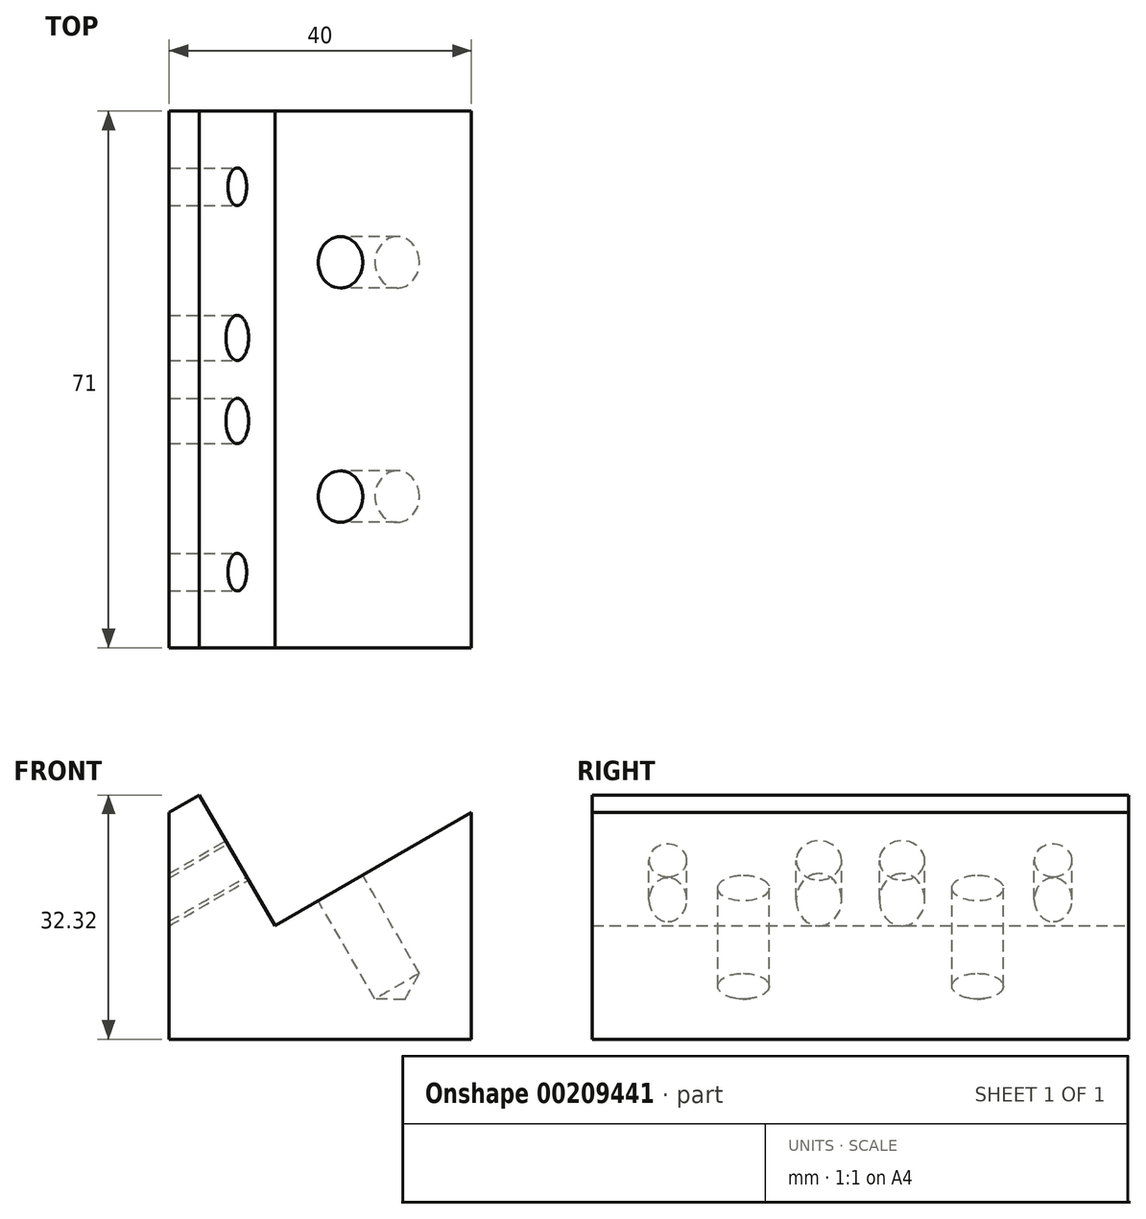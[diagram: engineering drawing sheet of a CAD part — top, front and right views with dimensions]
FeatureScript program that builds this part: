
annotation { "Feature Type Name" : "Feature", "Feature Type Description" : "" }
export const myFeature = defineFeature(function(context is Context, id is Id, definition is map)
    precondition{}
    {
        {
            var Q0;
            Q0=qCreatedBy(makeId("Front.planeOp"),FACE);
            var sketch = newSketch(context, id + "F0", { "sketchPlane" : qUnion([Q0])});
            skLineSegment(sketch, "E0", {"start": v(-41.74, 13.08) * mm, "end": v(-41.74, -16.92) * mm});
            skLineSegment(sketch, "E1", {"start": v(-41.74, -16.92) * mm, "end": v(-1.74, -16.92) * mm});
            skLineSegment(sketch, "E2", {"start": v(-1.74, -16.92) * mm, "end": v(-1.74, 13.08) * mm});
            skLineSegment(sketch, "E3", {"start": v(-1.74, 13.08) * mm, "end": v(-27.72, -1.92) * mm});
            skLineSegment(sketch, "E4", {"start": v(-27.72, -1.92) * mm, "end": v(-37.72, 15.4) * mm});
            skLineSegment(sketch, "E5", {"start": v(-37.72, 15.4) * mm, "end": v(-41.74, 13.08) * mm});
            skSolve(sketch);
        }
        {
            var Q0;
            Q0=makeQuery(id+"F0.imprint","IMPRINT",FACE,{"disambiguationData":[TD([[makeQuery(id+"F0.imprint","IMPRINT",EDGE,{"derivedFrom":sQuery(id+"F0.wireOp",EDGE,"E0")}),1.0]])]});
            extrude(context, id + "F1", {"entities" : qUnion([Q0]), "depth" : 71 * mm});
        }
        {
            var Q0;
            Q0=makeQuery(id+"F1.opExtrude","SWEPT_FACE",FACE,{"disambiguationData":[OSD([sQuery(id+"F0.wireOp",EDGE,"E3")])]});
            var sketch = newSketch(context, id + "F2", { "sketchPlane" : qUnion([Q0])});
            skPoint(sketch, "E6", {"position": v(-14.97, -20) * mm});
            skPoint(sketch, "E7", {"position": v(-14.97, -51) * mm});
            skSolve(sketch);
        }
        {
            var Q0;
            Q0=sQuery(id+"F2.wireOp",VERTEX,"E7");
            var Q1;
            Q1=sQuery(id+"F2.wireOp",VERTEX,"E6");
            var Q2;
            Q2=makeQuery(id+"F1.opExtrude","SWEPT_BODY",BODY,{"disambiguationData":[OSD([sQuery(id+"F0.wireOp",EDGE,"E0"),sQuery(id+"F0.wireOp",EDGE,"E1"),sQuery(id+"F0.wireOp",EDGE,"E2"),sQuery(id+"F0.wireOp",EDGE,"E3"),sQuery(id+"F0.wireOp",EDGE,"E4"),sQuery(id+"F0.wireOp",EDGE,"E5")])]});
            hole(context, id + "F3", {"style" : HoleStyle.SIMPLE, "endStyle" : HoleEndStyle.BLIND, "holeDiameter" : 6.8 * mm, "holeDepth" : 15 * mm, "locations" : qUnion([Q0, Q1]), "scope" : qUnion([Q2])});
        }
        {
            var Q0;
            Q0=makeQuery(id+"F1.opExtrude","SWEPT_FACE",FACE,{"disambiguationData":[OSD([sQuery(id+"F0.wireOp",EDGE,"E4")])]});
            var sketch = newSketch(context, id + "F4", { "sketchPlane" : qUnion([Q0])});
            skPoint(sketch, "E8", {"position": v(-61, 22.2) * mm});
            skPoint(sketch, "E9", {"position": v(-41, 22.2) * mm});
            skPoint(sketch, "E10", {"position": v(-30, 22.2) * mm});
            skPoint(sketch, "E11", {"position": v(-10, 22.2) * mm});
            skSolve(sketch);
        }
        {
            var Q0;
            Q0=sQuery(id+"F4.wireOp",VERTEX,"E9");
            var Q1;
            Q1=sQuery(id+"F4.wireOp",VERTEX,"E10");
            var Q2;
            Q2=makeQuery(id+"F1.opExtrude","SWEPT_BODY",BODY,{"disambiguationData":[OSD([sQuery(id+"F0.wireOp",EDGE,"E0"),sQuery(id+"F0.wireOp",EDGE,"E1"),sQuery(id+"F0.wireOp",EDGE,"E2"),sQuery(id+"F0.wireOp",EDGE,"E3"),sQuery(id+"F0.wireOp",EDGE,"E4"),sQuery(id+"F0.wireOp",EDGE,"E5")])]});
            hole(context, id + "F5", {"style" : HoleStyle.SIMPLE, "endStyle" : HoleEndStyle.THROUGH, "holeDiameter" : 6 * mm, "locations" : qUnion([Q0, Q1]), "scope" : qUnion([Q2]), "isTappedThrough" : true});
        }
        {
            var Q0;
            Q0=sQuery(id+"F4.wireOp",VERTEX,"E11");
            var Q1;
            Q1=sQuery(id+"F4.wireOp",VERTEX,"E8");
            var Q2;
            Q2=makeQuery(id+"F1.opExtrude","SWEPT_BODY",BODY,{"disambiguationData":[OSD([sQuery(id+"F0.wireOp",EDGE,"E0"),sQuery(id+"F0.wireOp",EDGE,"E1"),sQuery(id+"F0.wireOp",EDGE,"E2"),sQuery(id+"F0.wireOp",EDGE,"E3"),sQuery(id+"F0.wireOp",EDGE,"E4"),sQuery(id+"F0.wireOp",EDGE,"E5")])]});
            hole(context, id + "F6", {"style" : HoleStyle.SIMPLE, "endStyle" : HoleEndStyle.THROUGH, "holeDiameter" : 5 * mm, "locations" : qUnion([Q0, Q1]), "scope" : qUnion([Q2]), "isTappedThrough" : true});
        }
    });
